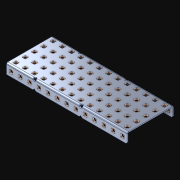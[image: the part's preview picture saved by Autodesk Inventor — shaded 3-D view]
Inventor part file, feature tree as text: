
AUTODESK INVENTOR PART (.ipt)
format: ipt  version: 2021 (Build 250183000, 183)  size: 1,748,992 bytes
history: native  units: in
note: dims shown in document units (in); Inventor stores cm internally (conversion verified against a paired STEP export)
features: extrude x92, other x92, sketch x4, pattern_linear x3
ambient origin geometry x8: Origin, YZ Plane, XZ Plane, XY Plane, X Axis, Y Axis, Z Axis, Center Point
bodies: Solid1 (feature_tree)
feature tree (191):
  pattern_linear  "Rectangular Pattern1"  Spacing1=0.182in  [1 undecoded]
  pattern_linear  "Rectangular Pattern2"  Spacing1=0.046in  [1 undecoded]
  pattern_linear  "Rectangular Pattern3"  Spacing1=0.5in  [1 undecoded]
  extrude  "Extrusion1"  Depth=0.046in
  sketch  "Sketch1"  dims[d0=0.182in]
  other  "Srf1"
  sketch  "Sketch2"  dims[d1=0.046in d2=0.0in]
  other  "Srf2"
  sketch  "Sketch3"  dims[d3=0.182in]
  other  "Srf3"
  other  "Srf4"
  other  "Srf5"
  other  "Srf6"
  other  "Srf7"
  other  "Srf8"
  other  "Srf9"
  other  "Srf10"
  other  "Srf11"
  other  "Srf12"
  other  "Srf13"
  other  "Srf14"
  other  "Srf15"
  other  "Srf38"
  other  "Srf39"
  other  "Srf40"
  other  "Srf41"
  other  "Srf42"
  other  "Srf43"
  other  "Srf44"
  other  "Srf45"
  other  "Srf46"
  other  "Srf47"
  other  "Srf48"
  other  "Srf49"
  other  "Srf72"
  other  "Srf73"
  other  "Srf74"
  other  "Srf75"
  other  "Srf76"
  other  "Srf77"
  other  "Srf78"
  other  "Srf79"
  other  "Srf80"
  other  "Srf81"
  other  "Srf82"
  other  "Srf83"
  other  "Srf84"
  other  "Srf107"
  other  "Srf108"
  other  "Srf109"
  other  "Srf110"
  other  "Srf111"
  other  "Srf112"
  other  "Srf113"
  other  "Srf114"
  other  "Srf115"
  other  "Srf116"
  other  "Srf117"
  other  "Srf118"
  other  "Srf119"
  other  "Srf142"
  other  "Srf143"
  other  "Srf144"
  other  "Srf145"
  other  "Srf146"
  other  "Srf147"
  other  "Srf148"
  other  "Srf149"
  other  "Srf150"
  other  "Srf151"
  other  "Srf152"
  other  "Srf153"
  other  "Srf154"
  other  "Srf177"
  other  "Srf178"
  other  "Srf179"
  other  "Srf180"
  other  "Srf181"
  other  "Srf182"
  other  "Srf183"
  other  "Srf184"
  other  "Srf185"
  other  "Srf186"
  other  "Srf187"
  other  "Srf188"
  other  "Srf189"
  other  "Srf212"
  other  "Srf213"
  other  "Srf214"
  other  "Srf215"
  other  "Srf216"
  other  "Srf217"
  other  "Srf218"
  other  "Srf219"
  other  "Srf220"
  other  "Srf221"
  other  "Srf222"
  other  "Srf223"
  sketch  "Sketch4"  dims[d4=0.046in d5=0.0in d6=0.182in d7=0.046in d8=0.0in d11=0.5in d12=5.1181in d14=0.5in d15=1.9685in d17=0.5in d18=5.1181in d20=0.5in d21=11.0in d22=0.0in]
  parser-record x1  (decoder bookkeeping rows leaked as tree rows — omitted from the tree; the rows remain in map.json)
  extrude  "ExtrusionSrf1"  Depth=0.046in
  extrude  "ExtrusionSrf2"  Depth=0.046in
  extrude  "ExtrusionSrf3"  Depth=0.046in
  extrude  "ExtrusionSrf4"  Depth=0.046in
  extrude  "ExtrusionSrf5"  Depth=0.046in
  extrude  "ExtrusionSrf6"  TaperAngle=0.0deg  [1 undecoded]
  extrude  "ExtrusionSrf7"  [1 undecoded]
  extrude  "ExtrusionSrf8"  [1 undecoded]
  extrude  "ExtrusionSrf9"  [1 undecoded]
  extrude  "ExtrusionSrf10"  [1 undecoded]
  extrude  "ExtrusionSrf11"  [1 undecoded]
  extrude  "ExtrusionSrf12"  [1 undecoded]
  extrude  "ExtrusionSrf13"  [1 undecoded]
  extrude  "ExtrusionSrf14"  [1 undecoded]
  extrude  "ExtrusionSrf15"  [1 undecoded]
  extrude  "ExtrusionSrf38"  [1 undecoded]
  extrude  "ExtrusionSrf39"  [1 undecoded]
  extrude  "ExtrusionSrf40"  [1 undecoded]
  extrude  "ExtrusionSrf41"  [1 undecoded]
  extrude  "ExtrusionSrf42"  [1 undecoded]
  extrude  "ExtrusionSrf43"  [1 undecoded]
  extrude  "ExtrusionSrf44"  [1 undecoded]
  extrude  "ExtrusionSrf45"  [1 undecoded]
  extrude  "ExtrusionSrf46"  [1 undecoded]
  extrude  "ExtrusionSrf47"  [1 undecoded]
  extrude  "ExtrusionSrf48"  [1 undecoded]
  extrude  "ExtrusionSrf49"  [1 undecoded]
  extrude  "ExtrusionSrf72"  [1 undecoded]
  extrude  "ExtrusionSrf73"  [1 undecoded]
  extrude  "ExtrusionSrf74"  [1 undecoded]
  extrude  "ExtrusionSrf75"  [1 undecoded]
  extrude  "ExtrusionSrf76"  [1 undecoded]
  extrude  "ExtrusionSrf77"  [1 undecoded]
  extrude  "ExtrusionSrf78"  [1 undecoded]
  extrude  "ExtrusionSrf79"  [1 undecoded]
  extrude  "ExtrusionSrf80"  [1 undecoded]
  extrude  "ExtrusionSrf81"  [1 undecoded]
  extrude  "ExtrusionSrf82"  [1 undecoded]
  extrude  "ExtrusionSrf83"  [1 undecoded]
  extrude  "ExtrusionSrf84"  [1 undecoded]
  extrude  "ExtrusionSrf107"  [1 undecoded]
  extrude  "ExtrusionSrf108"  [1 undecoded]
  extrude  "ExtrusionSrf109"  [1 undecoded]
  extrude  "ExtrusionSrf110"  [1 undecoded]
  extrude  "ExtrusionSrf111"  [1 undecoded]
  extrude  "ExtrusionSrf112"  [1 undecoded]
  extrude  "ExtrusionSrf113"  [1 undecoded]
  extrude  "ExtrusionSrf114"  [1 undecoded]
  extrude  "ExtrusionSrf115"  [1 undecoded]
  extrude  "ExtrusionSrf116"  [1 undecoded]
  extrude  "ExtrusionSrf117"  [1 undecoded]
  extrude  "ExtrusionSrf118"  [1 undecoded]
  extrude  "ExtrusionSrf119"  [1 undecoded]
  extrude  "ExtrusionSrf142"  [1 undecoded]
  extrude  "ExtrusionSrf143"  [1 undecoded]
  extrude  "ExtrusionSrf144"  [1 undecoded]
  extrude  "ExtrusionSrf145"  [1 undecoded]
  extrude  "ExtrusionSrf146"  [1 undecoded]
  extrude  "ExtrusionSrf147"  [1 undecoded]
  extrude  "ExtrusionSrf148"  [1 undecoded]
  extrude  "ExtrusionSrf149"  [1 undecoded]
  extrude  "ExtrusionSrf150"  [1 undecoded]
  extrude  "ExtrusionSrf151"  [1 undecoded]
  extrude  "ExtrusionSrf152"  [1 undecoded]
  extrude  "ExtrusionSrf153"  [1 undecoded]
  extrude  "ExtrusionSrf154"  [1 undecoded]
  extrude  "ExtrusionSrf177"  [1 undecoded]
  extrude  "ExtrusionSrf178"  [1 undecoded]
  extrude  "ExtrusionSrf179"  [1 undecoded]
  extrude  "ExtrusionSrf180"  [1 undecoded]
  extrude  "ExtrusionSrf181"  [1 undecoded]
  extrude  "ExtrusionSrf182"  [1 undecoded]
  extrude  "ExtrusionSrf183"  [1 undecoded]
  extrude  "ExtrusionSrf184"  [1 undecoded]
  extrude  "ExtrusionSrf185"  [1 undecoded]
  extrude  "ExtrusionSrf186"  [1 undecoded]
  extrude  "ExtrusionSrf187"  [1 undecoded]
  extrude  "ExtrusionSrf188"  [1 undecoded]
  extrude  "ExtrusionSrf189"  [1 undecoded]
  extrude  "ExtrusionSrf212"  [1 undecoded]
  extrude  "ExtrusionSrf213"  [1 undecoded]
  extrude  "ExtrusionSrf214"  [1 undecoded]
  extrude  "ExtrusionSrf215"  [1 undecoded]
  extrude  "ExtrusionSrf216"  [1 undecoded]
  extrude  "ExtrusionSrf217"  [1 undecoded]
  extrude  "ExtrusionSrf218"  [1 undecoded]
  extrude  "ExtrusionSrf219"  [1 undecoded]
  extrude  "ExtrusionSrf220"  [1 undecoded]
  extrude  "ExtrusionSrf221"  [1 undecoded]
  extrude  "ExtrusionSrf222"  [1 undecoded]
  extrude  "ExtrusionSrf223"  [1 undecoded]
note: 89 required parameter values undecoded (feature->parameter linkage not recoverable at this tier; creation-order binding heuristic only, values carry confidence <= 0.55)
